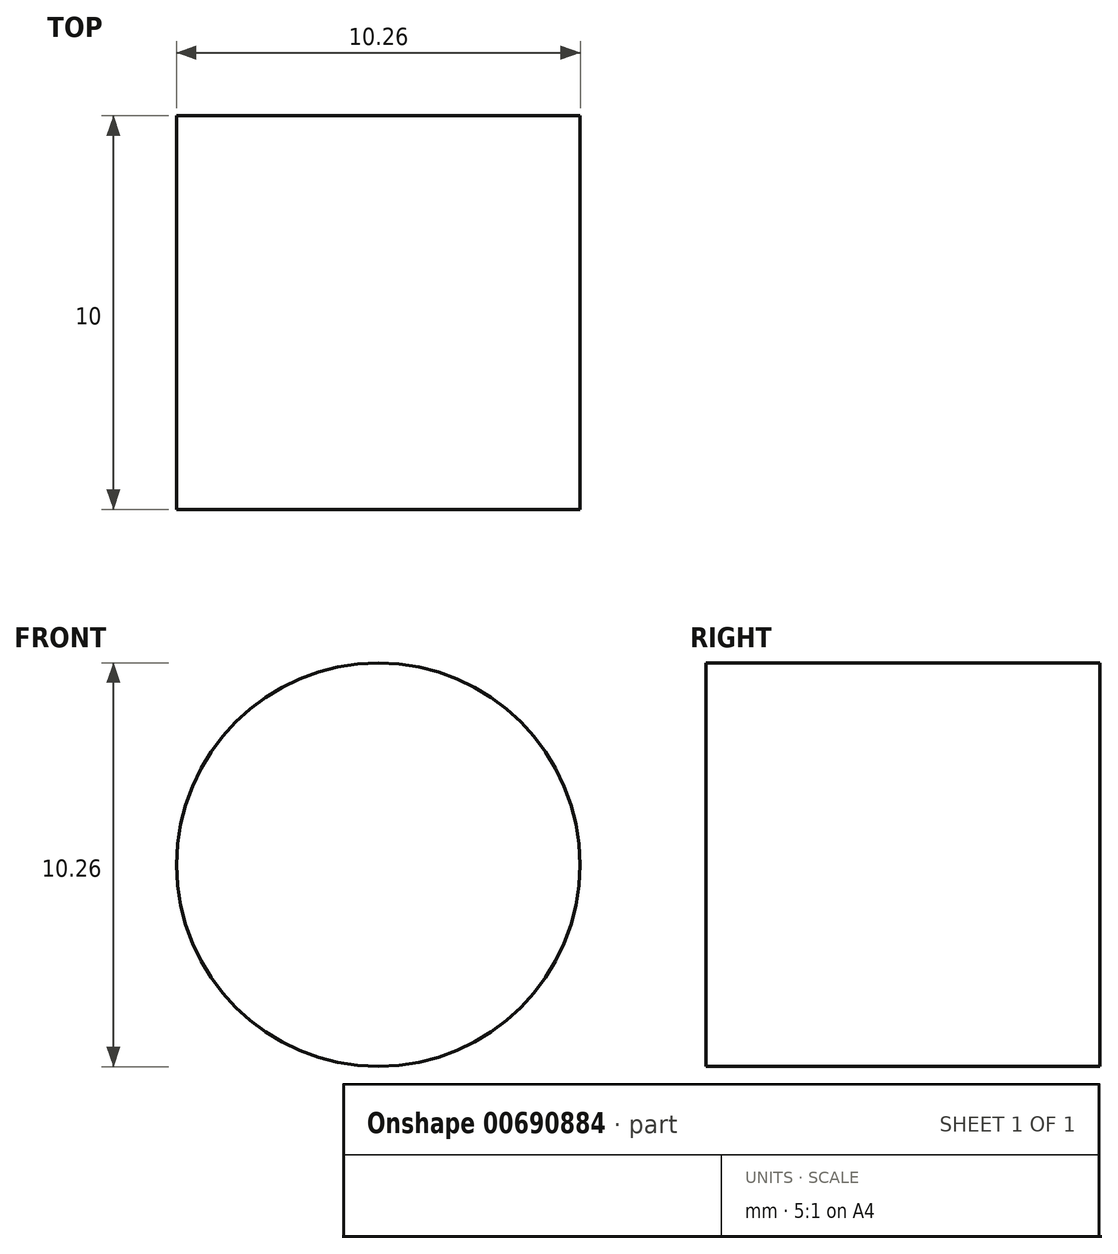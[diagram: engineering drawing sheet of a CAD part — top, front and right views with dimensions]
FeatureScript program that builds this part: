
annotation { "Feature Type Name" : "Feature", "Feature Type Description" : "" }
export const myFeature = defineFeature(function(context is Context, id is Id, definition is map)
    precondition{}
    {
        {
            var Q0;
            Q0=qCreatedBy(makeId("Front.planeOp"),FACE);
            var sketch = newSketch(context, id + "F0", { "sketchPlane" : qUnion([Q0])});
            skCircle(sketch, "E0", {"center": v(0, 0) * mm, "radius": 5.12 * mm});
            skSolve(sketch);
        }
        {
            var Q0;
            Q0 = qSketchRegion(id + "F0", true);
            extrude(context, id + "F1", {"entities" : qUnion([Q0]), "depth" : 10 * mm, "offsetDistance" : 25 * mm});
        }
    });
